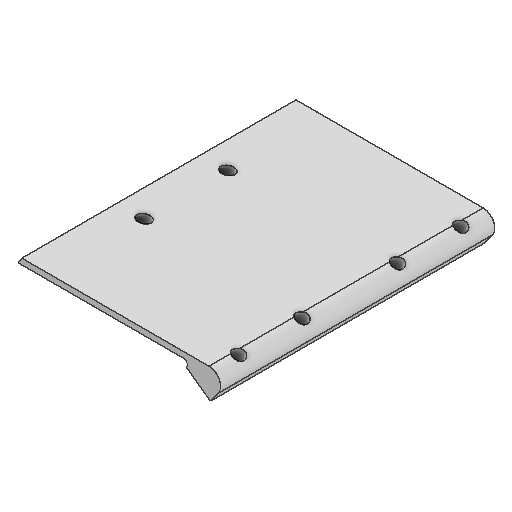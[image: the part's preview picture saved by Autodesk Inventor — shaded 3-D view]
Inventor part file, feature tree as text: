
AUTODESK INVENTOR PART (.ipt)
format: ipt  version: 2025 (Build 290162000, 162)  size: 230,400 bytes
history: native  units: mm
features: extrude x8, sketch x8, reference x8, projected_geometry x8, other x7, fillet x2, plane x2, mirror x1
ambient origin geometry x8: Origin, YZ Plane, XZ Plane, XY Plane, X Axis, Y Axis, Z Axis, Center Point
bodies: Solid1 (feature_tree)
feature tree (44):
  extrude  "Extrusion1"  Depth=120.0mm
  extrude  "Extrusion2"  TaperAngle=0.0deg  [1 undecoded]
  extrude  "Extrusion3"  Depth=10.0mm
  fillet  "Fillet1"  Radius=44.45mm
  extrude  "Extrusion4"  Depth=101.6mm TaperAngle=0.0deg
  fillet  "Fillet2"  Radius=5.5mm
  mirror  "Mirror1"
  extrude  "Extrusion5"  [1 undecoded]
  extrude  "Extrusion6"  Depth=10.0mm
  plane  "Work Plane1"
  extrude  "Extrusion7"  [1 undecoded]
  plane  "Work Plane2"
  extrude  "Extrusion8"  TaperAngle=0.0deg  [1 undecoded]
  sketch  "Sketch1"  dims[d0=234.0mm d1=120.0mm]
  sketch  "Sketch2"  dims[d2=5.0mm d3=0.0mm d4=0.0mm d5=0.0mm]
  reference  "Reference1"
  projected_geometry  "Projected Loop1"
  sketch  "Sketch3"  dims[d6=10.0mm d7=0.0mm d8=10.0mm d9=44.45mm d10=0.0mm]
  projected_geometry  "Projected Loop2"
  reference  "Reference2"
  reference  "Reference3"
  reference  "Reference4"
  reference  "Reference5"
  sketch  "Sketch4"  dims[d11=3.0mm d12=101.6mm d13=0.0mm d14=5.5mm]
  projected_geometry  "Projected Loop3"
  sketch  "Sketch5"  dims[d15=0.0mm d16=0.0mm d17=-5.0mm]
  projected_geometry  "Projected Loop4"
  reference  "Reference6"
  reference  "Reference7"
  reference  "Reference8"
  sketch  "Sketch6"  dims[d18=10.0mm d19=10.0mm]
  projected_geometry  "Projected Loop5"
  projected_geometry  "Projected Loop6"
  sketch  "Sketch7"  dims[d20=0.0mm d21=0.0mm d22=-5.0mm]
  projected_geometry  "Projected Loop7"
  sketch  "Sketch8"  dims[d23=10.0mm d24=0.0mm d25=0.0mm]
  projected_geometry  "Projected Loop8"
  other  "<userpath>\Desktop\puppycat\woodhouseMK1.iam"
  other  "woodhouseMK1.iam"
  other  "lowerSkidPlateRear:1"
  other  "12inStrut:1"
  other  "hoverboardMotorMount:2"
  other  "upperRearBracketFlipped:1"
  other  "lowerRearBracketFlipped:1"
note: 4 required parameter values undecoded (feature->parameter linkage not recoverable at this tier; creation-order binding heuristic only, values carry confidence <= 0.55)
